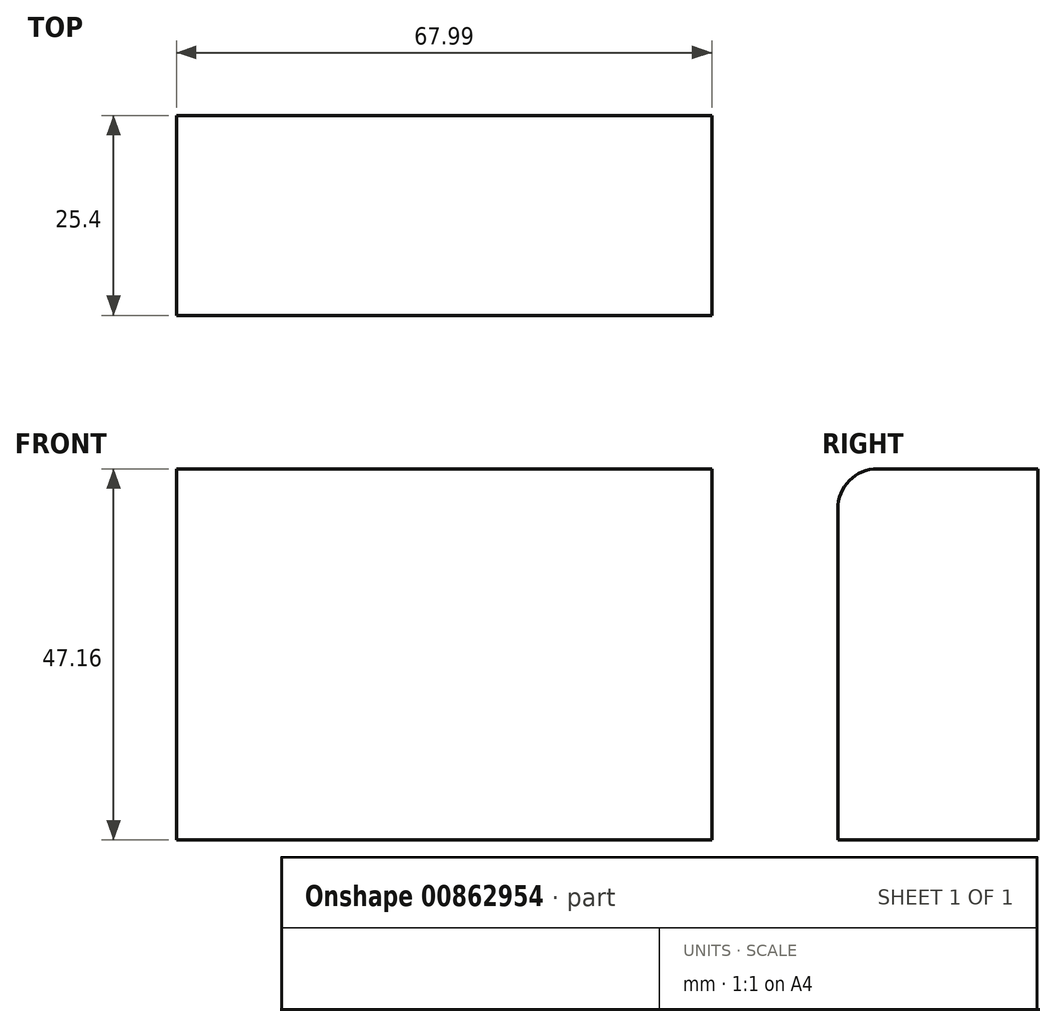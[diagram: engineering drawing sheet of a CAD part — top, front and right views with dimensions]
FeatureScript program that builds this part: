
annotation { "Feature Type Name" : "Feature", "Feature Type Description" : "" }
export const myFeature = defineFeature(function(context is Context, id is Id, definition is map)
    precondition{}
    {
        {
            var Q0;
            Q0=qCreatedBy(makeId("Front.planeOp"),FACE);
            var sketch = newSketch(context, id + "F0", { "sketchPlane" : qUnion([Q0])});
            skLineSegment(sketch, "E0.bottom", {"start": v(0, 0) * mm, "end": v(-68, 0) * mm});
            skLineSegment(sketch, "E0.top", {"start": v(0, 47.16) * mm, "end": v(-68, 47.16) * mm});
            skLineSegment(sketch, "E0.left", {"start": v(0, 0) * mm, "end": v(0, 47.16) * mm});
            skLineSegment(sketch, "E0.right", {"start": v(-68, 0) * mm, "end": v(-68, 47.16) * mm});
            skSolve(sketch);
        }
        {
            var Q0;
            Q0 = qSketchRegion(id + "F0", true);
            extrude(context, id + "F1", {"entities" : qUnion([Q0]), "depth" : 25.4 * mm, "offsetDistance" : 25.4 * mm});
        }
        {
            var Q0;
            Q0=makeQuery(id+"F1.opExtrude","CAP_EDGE",EDGE,{"disambiguationData":[OSD([sQuery(id+"F0.wireOp",EDGE,"E0.top")])],"isStart":false});
            fillet(context, id + "F2", {"entities" : qUnion([Q0]), "radius" : 5.08 * mm, "tangentPropagation" : true, "allowEdgeOverflow" : false});
        }
    });
